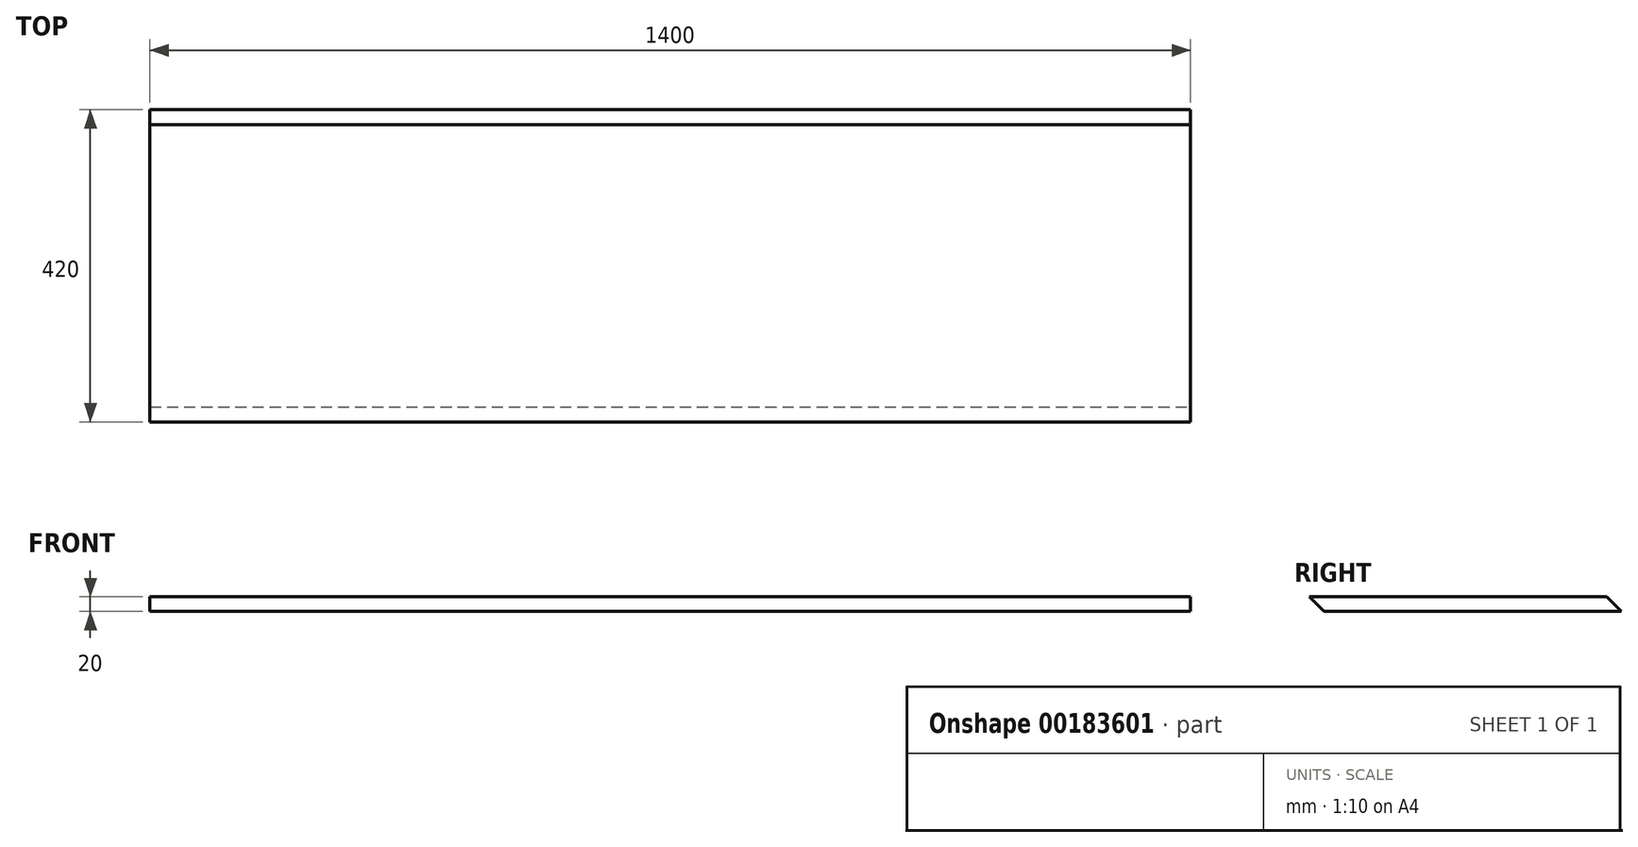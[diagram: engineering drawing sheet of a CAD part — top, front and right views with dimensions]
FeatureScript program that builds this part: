
annotation { "Feature Type Name" : "Feature", "Feature Type Description" : "" }
export const myFeature = defineFeature(function(context is Context, id is Id, definition is map)
    precondition{}
    {
        {
            var Q0;
            Q0=qCreatedBy(makeId("Top.planeOp"),FACE);
            var sketch = newSketch(context, id + "F0", { "sketchPlane" : qUnion([Q0])});
            skLineSegment(sketch, "E0.bottom", {"start": v(700, 210) * mm, "end": v(-700, 210) * mm});
            skLineSegment(sketch, "E0.top", {"start": v(700, -210) * mm, "end": v(-700, -210) * mm});
            skLineSegment(sketch, "E0.left", {"start": v(700, 210) * mm, "end": v(700, -210) * mm});
            skLineSegment(sketch, "E0.right", {"start": v(-700, 210) * mm, "end": v(-700, -210) * mm});
            skPoint(sketch, "E0.middle", {"position": v(0, 0) * mm});
            skSolve(sketch);
        }
        {
            var Q0;
            Q0 = qSketchRegion(id + "F0", true);
            extrude(context, id + "F1", {"entities" : qUnion([Q0]), "depth" : 20 * mm});
        }
        {
            var Q0;
            Q0=makeQuery(id+"F1.opExtrude","SWEPT_FACE",FACE,{"disambiguationData":[OSD([sQuery(id+"F0.wireOp",EDGE,"E0.left")])]});
            var sketch = newSketch(context, id + "F2", { "sketchPlane" : qUnion([Q0])});
            skLineSegment(sketch, "E1", {"start": v(-210, 20) * mm, "end": v(-190, 0) * mm});
            skLineSegment(sketch, "E2", {"start": v(-190, 0) * mm, "end": v(-210, 0) * mm});
            skLineSegment(sketch, "E3", {"start": v(-210, 0) * mm, "end": v(-210, 20) * mm});
            skLineSegment(sketch, "E4", {"start": v(210, 0) * mm, "end": v(210, 20) * mm});
            skLineSegment(sketch, "E5", {"start": v(210, 20) * mm, "end": v(190, 20) * mm});
            skLineSegment(sketch, "E6", {"start": v(190, 20) * mm, "end": v(210, 0) * mm});
            skSolve(sketch);
        }
        {
            var Q0;
            Q0 = qSketchRegion(id + "F2", true);
            extrude(context, id + "F3", {"entities" : qUnion([Q0]), "operationType" : NewBodyOperationType.REMOVE, "oppositeDirection" : true, "depth" : 1400 * mm});
        }
    });
